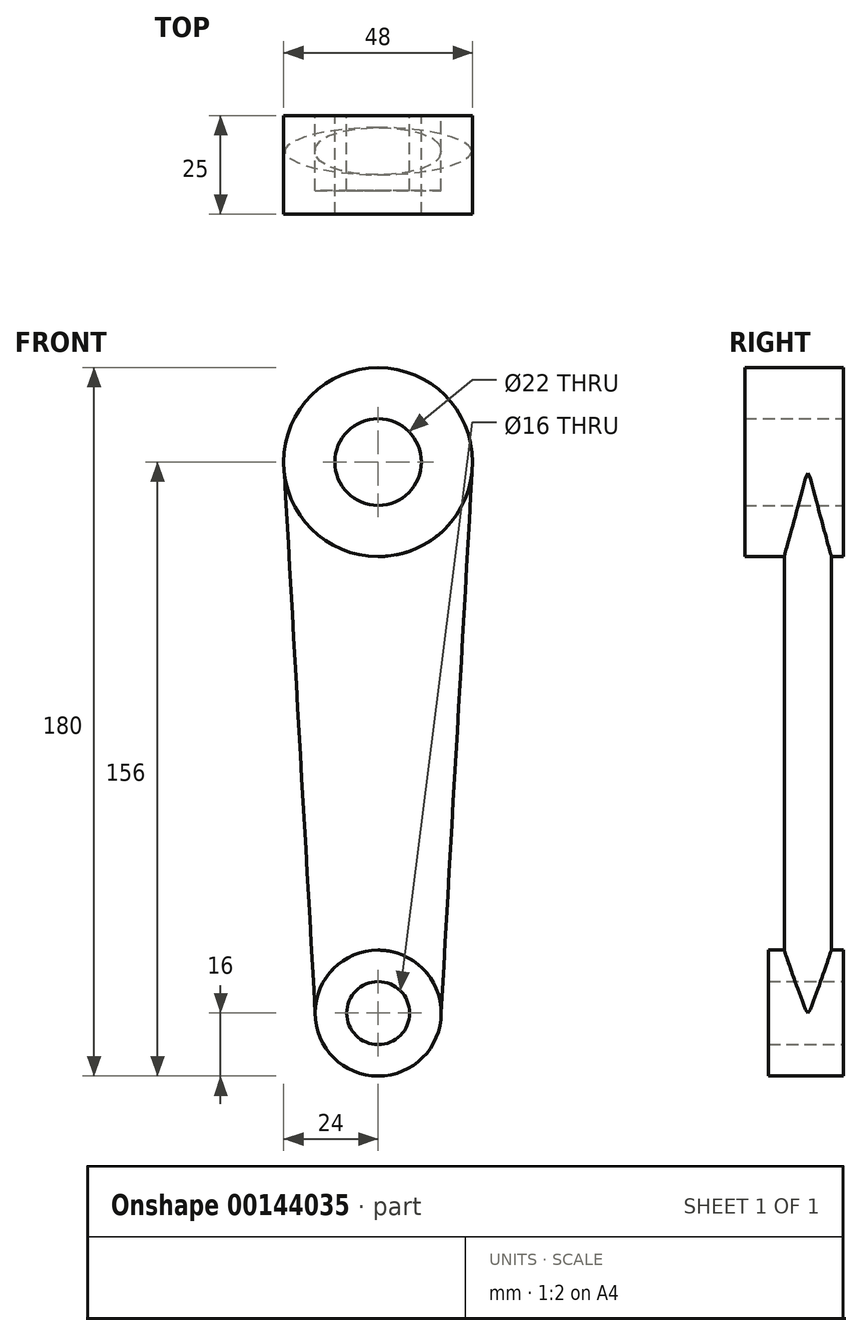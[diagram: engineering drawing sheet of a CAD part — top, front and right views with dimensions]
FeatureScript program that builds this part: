
annotation { "Feature Type Name" : "Feature", "Feature Type Description" : "" }
export const myFeature = defineFeature(function(context is Context, id is Id, definition is map)
    precondition{}
    {
        {
            var Q0;
            Q0=qCreatedBy(makeId("Front.planeOp"),FACE);
            var sketch = newSketch(context, id + "F0", { "sketchPlane" : qUnion([Q0])});
            skCircle(sketch, "E0", {"center": v(0, 0) * mm, "radius": 16 * mm});
            skCircle(sketch, "E1", {"center": v(0, 140) * mm, "radius": 24 * mm});
            skLineSegment(sketch, "E2", {"start": v(0, 0) * mm, "end": v(0, 140) * mm, "construction": true});
            skCircle(sketch, "E3", {"center": v(0, 140) * mm, "radius": 11 * mm});
            skCircle(sketch, "E4", {"center": v(0, 0) * mm, "radius": 8 * mm});
            skSolve(sketch);
        }
        {
            var Q0;
            Q0=makeQuery(id+"F0.imprint","IMPRINT",FACE,{"disambiguationData":[TD([[makeQuery(id+"F0.imprint","IMPRINT",EDGE,{"derivedFrom":sQuery(id+"F0.wireOp",EDGE,"E0")}),1.0]])]});
            var Q1;
            Q1=makeQuery(id+"F0.imprint","IMPRINT",FACE,{"disambiguationData":[TD([[makeQuery(id+"F0.imprint","IMPRINT",EDGE,{"derivedFrom":sQuery(id+"F0.wireOp",EDGE,"E4")}),1.0]])]});
            extrude(context, id + "F1", {"entities" : qUnion([Q0, Q1]), "depth" : 19 * mm});
        }
        {
            var Q0;
            Q0=makeQuery(id+"F0.imprint","IMPRINT",FACE,{"disambiguationData":[TD([[makeQuery(id+"F0.imprint","IMPRINT",EDGE,{"derivedFrom":sQuery(id+"F0.wireOp",EDGE,"E1")}),1.0]])]});
            var Q1;
            Q1=makeQuery(id+"F0.imprint","IMPRINT",FACE,{"disambiguationData":[TD([[makeQuery(id+"F0.imprint","IMPRINT",EDGE,{"derivedFrom":sQuery(id+"F0.wireOp",EDGE,"E3")}),1.0]])]});
            extrude(context, id + "F2", {"entities" : qUnion([Q0, Q1]), "depth" : 25 * mm});
        }
        {
            var Q0;
            Q0=qCreatedBy(makeId("Top.planeOp"),FACE);
            var sketch = newSketch(context, id + "F3", { "sketchPlane" : qUnion([Q0])});
            skEllipse(sketch, "E5", {"center": v(0, -9) * mm, "majorRadius": 16 * mm, "minorRadius": 6 * mm, "majorAxis": v(1, 0)});
            skPoint(sketch, "E6", {"position": v(0, -3) * mm});
            skLineSegment(sketch, "E7", {"start": v(16, 0) * mm, "end": v(16, -19) * mm, "construction": true});
            skSolve(sketch);
        }
        {
            var Q0;
            Q0=sQuery(id+"F0.wireOp",VERTEX,"E3.center");
            var Q1;
            Q1=qCreatedBy(makeId("Top.planeOp"),FACE);
            cPlane(context, id + "F4", {"entities" : qUnion([Q0, Q1]), "cplaneType" : CPlaneType.PLANE_POINT, "offset" : 25 * mm, "width" : 150 * mm, "height" : 150 * mm});
        }
        {
            var Q0;
            Q0=qCreatedBy(id+"F4.planeOp",FACE);
            var sketch = newSketch(context, id + "F5", { "sketchPlane" : qUnion([Q0])});
            skEllipse(sketch, "E8", {"center": v(0, -9) * mm, "majorRadius": 24 * mm, "minorRadius": 6 * mm, "majorAxis": v(1, 0)});
            skPoint(sketch, "E9", {"position": v(0, -3) * mm});
            skLineSegment(sketch, "E10", {"start": v(24, 0) * mm, "end": v(24, -25) * mm, "construction": true});
            skSolve(sketch);
        }
        {
            var Q0;
            Q0=makeQuery(id+"F5.imprint","IMPRINT",FACE,{"disambiguationData":[TD([[makeQuery(id+"F5.imprint","IMPRINT",EDGE,{"derivedFrom":sQuery(id+"F5.wireOp",EDGE,"E8")}),1.0]])]});
            var Q1;
            Q1=makeQuery(id+"F3.imprint","IMPRINT",FACE,{"disambiguationData":[TD([[makeQuery(id+"F3.imprint","IMPRINT",EDGE,{"derivedFrom":sQuery(id+"F3.wireOp",EDGE,"E5")}),1.0]])]});
            loft(context, id + "F6", {"operationType" : NewBodyOperationType.ADD, "sheetProfilesArray" : [{ "sheetProfileEntities" : qUnion([Q0]) }, { "sheetProfileEntities" : qUnion([Q1]) }]});
        }
        {
            var Q0;
            Q0=makeQuery(id+"F0.imprint","IMPRINT",FACE,{"disambiguationData":[TD([[makeQuery(id+"F0.imprint","IMPRINT",EDGE,{"derivedFrom":sQuery(id+"F0.wireOp",EDGE,"E3")}),1.0]])]});
            var Q1;
            Q1=makeQuery(id+"F0.imprint","IMPRINT",FACE,{"disambiguationData":[TD([[makeQuery(id+"F0.imprint","IMPRINT",EDGE,{"derivedFrom":sQuery(id+"F0.wireOp",EDGE,"E4")}),1.0]])]});
            extrude(context, id + "F7", {"entities" : qUnion([Q0, Q1]), "operationType" : NewBodyOperationType.REMOVE, "endBound" : BoundingType.THROUGH_ALL, "depth" : 25 * mm});
        }
    });
